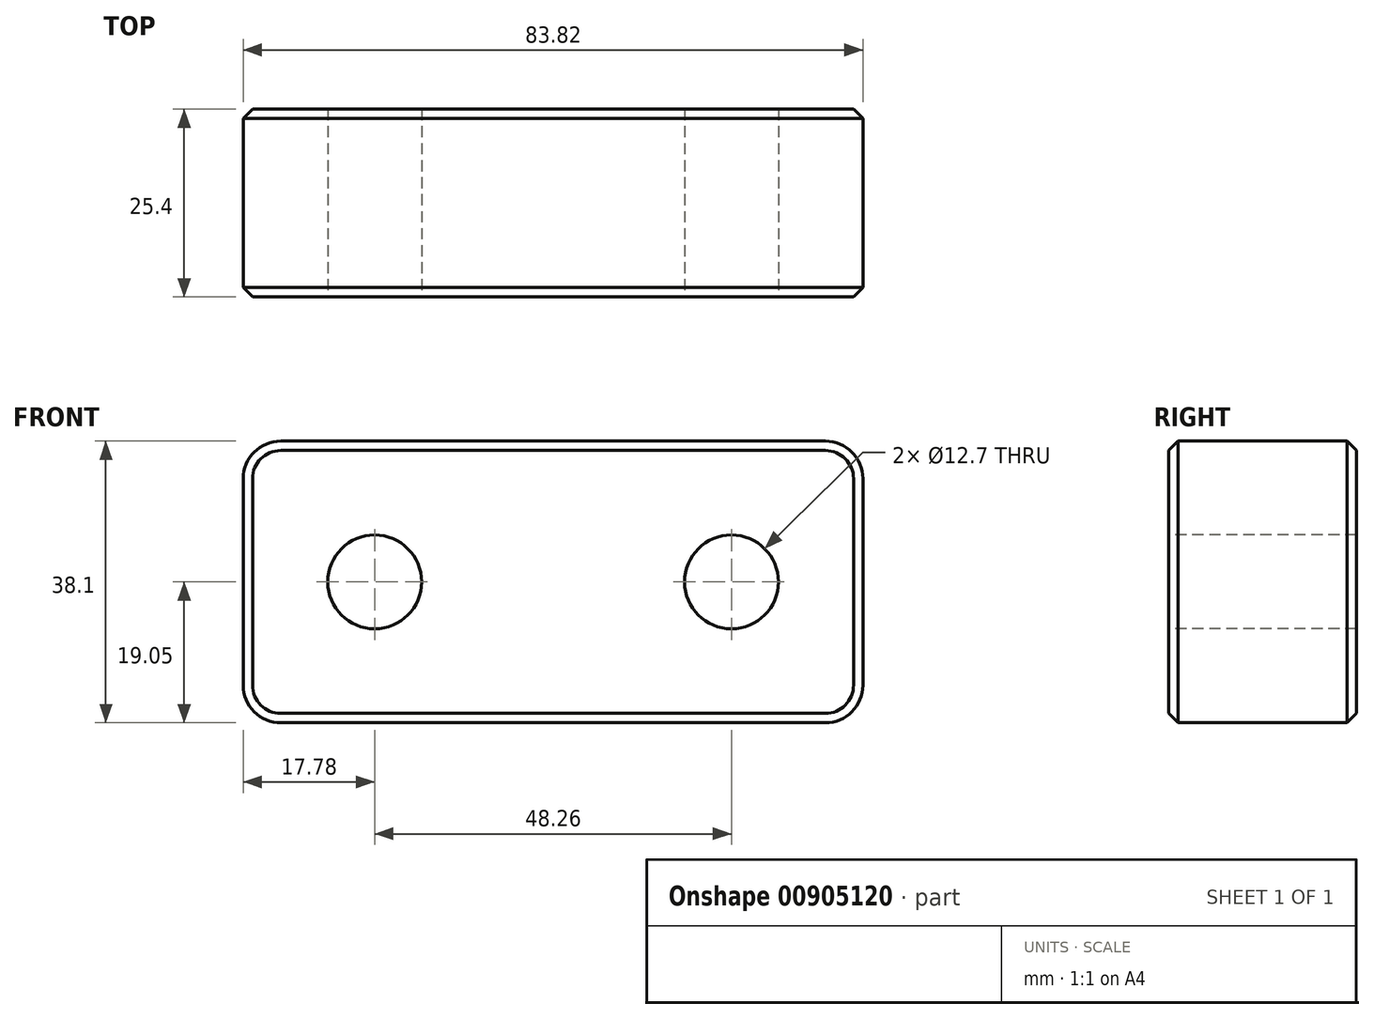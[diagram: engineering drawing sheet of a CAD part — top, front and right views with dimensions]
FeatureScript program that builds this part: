
annotation { "Feature Type Name" : "Feature", "Feature Type Description" : "" }
export const myFeature = defineFeature(function(context is Context, id is Id, definition is map)
    precondition{}
    {
        {
            var Q0;
            Q0=qCreatedBy(makeId("Front.planeOp"),FACE);
            var sketch = newSketch(context, id + "F0", { "sketchPlane" : qUnion([Q0])});
            skLineSegment(sketch, "E0.bottom", {"start": v(0, 0) * mm, "end": v(83.82, 0) * mm});
            skLineSegment(sketch, "E0.top", {"start": v(0, 38.1) * mm, "end": v(83.82, 38.1) * mm});
            skLineSegment(sketch, "E0.left", {"start": v(0, 0) * mm, "end": v(0, 38.1) * mm});
            skLineSegment(sketch, "E0.right", {"start": v(83.82, 0) * mm, "end": v(83.82, 38.1) * mm});
            skSolve(sketch);
        }
        {
            var Q0;
            Q0=makeQuery(id+"F0.imprint","IMPRINT",FACE,{"disambiguationData":[TD([[makeQuery(id+"F0.imprint","IMPRINT",EDGE,{"derivedFrom":sQuery(id+"F0.wireOp",EDGE,"E0.bottom")}),1.0]])]});
            extrude(context, id + "F1", {"entities" : qUnion([Q0]), "depth" : 25.4 * mm, "offsetDistance" : 25.4 * mm});
        }
        {
            var Q0;
            Q0=makeQuery(id+"F1.opExtrude","SWEPT_EDGE",EDGE,{"disambiguationData":[OSD([sQuery(id+"F0.wireOp",EDGE,"E0.top"),sQuery(id+"F0.wireOp",EDGE,"E0.right")])]});
            var Q1;
            Q1=makeQuery(id+"F1.opExtrude","SWEPT_EDGE",EDGE,{"disambiguationData":[OSD([sQuery(id+"F0.wireOp",EDGE,"E0.top"),sQuery(id+"F0.wireOp",EDGE,"E0.left")])]});
            var Q2;
            Q2=makeQuery(id+"F1.opExtrude","SWEPT_EDGE",EDGE,{"disambiguationData":[OSD([sQuery(id+"F0.wireOp",EDGE,"E0.bottom"),sQuery(id+"F0.wireOp",EDGE,"E0.right")])]});
            var Q3;
            Q3=makeQuery(id+"F1.opExtrude","SWEPT_EDGE",EDGE,{"disambiguationData":[OSD([sQuery(id+"F0.wireOp",EDGE,"E0.bottom"),sQuery(id+"F0.wireOp",EDGE,"E0.left")])]});
            fillet(context, id + "F2", {"entities" : qUnion([Q0, Q1, Q2, Q3]), "radius" : 5.08 * mm, "tangentPropagation" : true, "allowEdgeOverflow" : false});
        }
        {
            var Q0;
            Q0=makeQuery(id+"F1.opExtrude","CAP_FACE",FACE,{"disambiguationData":[OSD([sQuery(id+"F0.wireOp",EDGE,"E0.bottom"),sQuery(id+"F0.wireOp",EDGE,"E0.top"),sQuery(id+"F0.wireOp",EDGE,"E0.left"),sQuery(id+"F0.wireOp",EDGE,"E0.right")])],"isStart":false});
            var sketch = newSketch(context, id + "F3", { "sketchPlane" : qUnion([Q0])});
            skCircle(sketch, "E1", {"center": v(17.78, 19.05) * mm, "radius": 6.35 * mm});
            skPoint(sketch, "E1.centerSnap0", {"position": v(0, 19.05) * mm});
            skCircle(sketch, "E2", {"center": v(66.04, 19.05) * mm, "radius": 6.35 * mm});
            skPoint(sketch, "E2.centerSnap0", {"position": v(83.82, 19.05) * mm});
            skSolve(sketch);
        }
        {
            var Q0;
            Q0=makeQuery(id+"F3.imprint","IMPRINT",FACE,{"disambiguationData":[TD([[makeQuery(id+"F3.imprint","IMPRINT",EDGE,{"derivedFrom":sQuery(id+"F3.wireOp",EDGE,"E1")}),1.0]])]});
            var Q1;
            Q1=makeQuery(id+"F3.imprint","IMPRINT",FACE,{"disambiguationData":[TD([[makeQuery(id+"F3.imprint","IMPRINT",EDGE,{"derivedFrom":sQuery(id+"F3.wireOp",EDGE,"E2")}),1.0]])]});
            extrude(context, id + "F4", {"entities" : qUnion([Q0, Q1]), "operationType" : NewBodyOperationType.REMOVE, "endBound" : BoundingType.UP_TO_NEXT, "oppositeDirection" : true, "depth" : 25.4 * mm, "offsetDistance" : 25.4 * mm});
        }
        {
            var Q0;
            Q0=makeQuery(id+"F1.opExtrude","CAP_EDGE",EDGE,{"disambiguationData":[OSD([sQuery(id+"F0.wireOp",EDGE,"E0.top")])],"isStart":false});
            var Q1;
            Q1=makeQuery(id+"F1.opExtrude","CAP_EDGE",EDGE,{"disambiguationData":[OSD([sQuery(id+"F0.wireOp",EDGE,"E0.top")])],"isStart":true});
            chamfer(context, id + "F5", {"entities" : qUnion([Q0, Q1]), "width" : 1.27 * mm, "tangentPropagation" : true});
        }
    });
